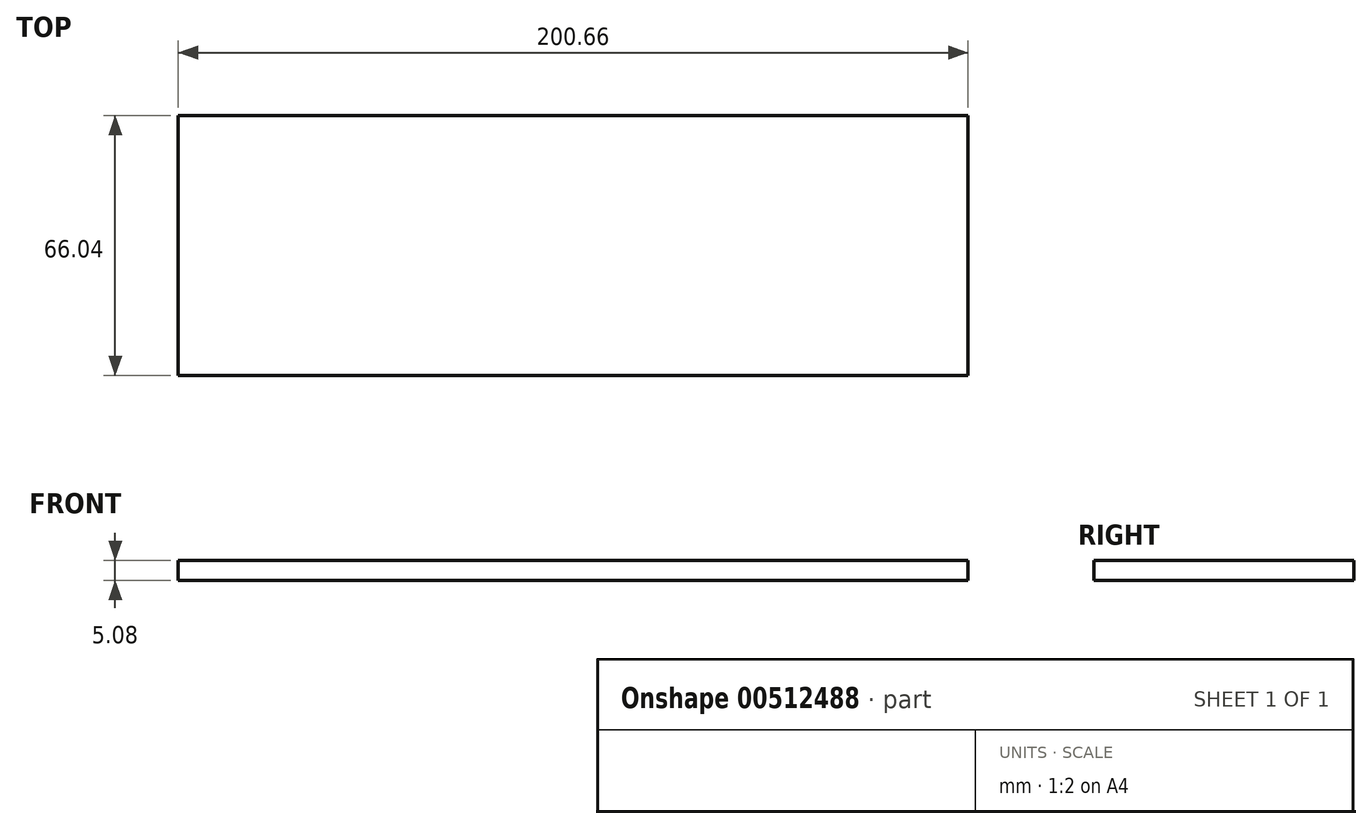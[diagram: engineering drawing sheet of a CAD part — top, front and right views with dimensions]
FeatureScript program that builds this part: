
annotation { "Feature Type Name" : "Feature", "Feature Type Description" : "" }
export const myFeature = defineFeature(function(context is Context, id is Id, definition is map)
    precondition{}
    {
        {
            var Q0;
            Q0=qCreatedBy(makeId("Top.planeOp"),FACE);
            var sketch = newSketch(context, id + "F0", { "sketchPlane" : qUnion([Q0])});
            skLineSegment(sketch, "E0.bottom", {"start": v(-56.92, 23.23) * mm, "end": v(143.74, 23.23) * mm});
            skLineSegment(sketch, "E0.top", {"start": v(-56.92, -42.8) * mm, "end": v(143.74, -42.8) * mm});
            skLineSegment(sketch, "E0.left", {"start": v(-56.92, 23.23) * mm, "end": v(-56.92, -42.8) * mm});
            skLineSegment(sketch, "E0.right", {"start": v(143.74, 23.23) * mm, "end": v(143.74, -42.8) * mm});
            skSolve(sketch);
        }
        {
            var Q0;
            Q0=makeQuery(id+"F0.imprint","IMPRINT",FACE,{"disambiguationData":[TD([[makeQuery(id+"F0.imprint","IMPRINT",EDGE,{"derivedFrom":sQuery(id+"F0.wireOp",EDGE,"E0.bottom")}),-1.0]])]});
            extrude(context, id + "F1", {"entities" : qUnion([Q0]), "depth" : 5.08 * mm});
        }
    });
